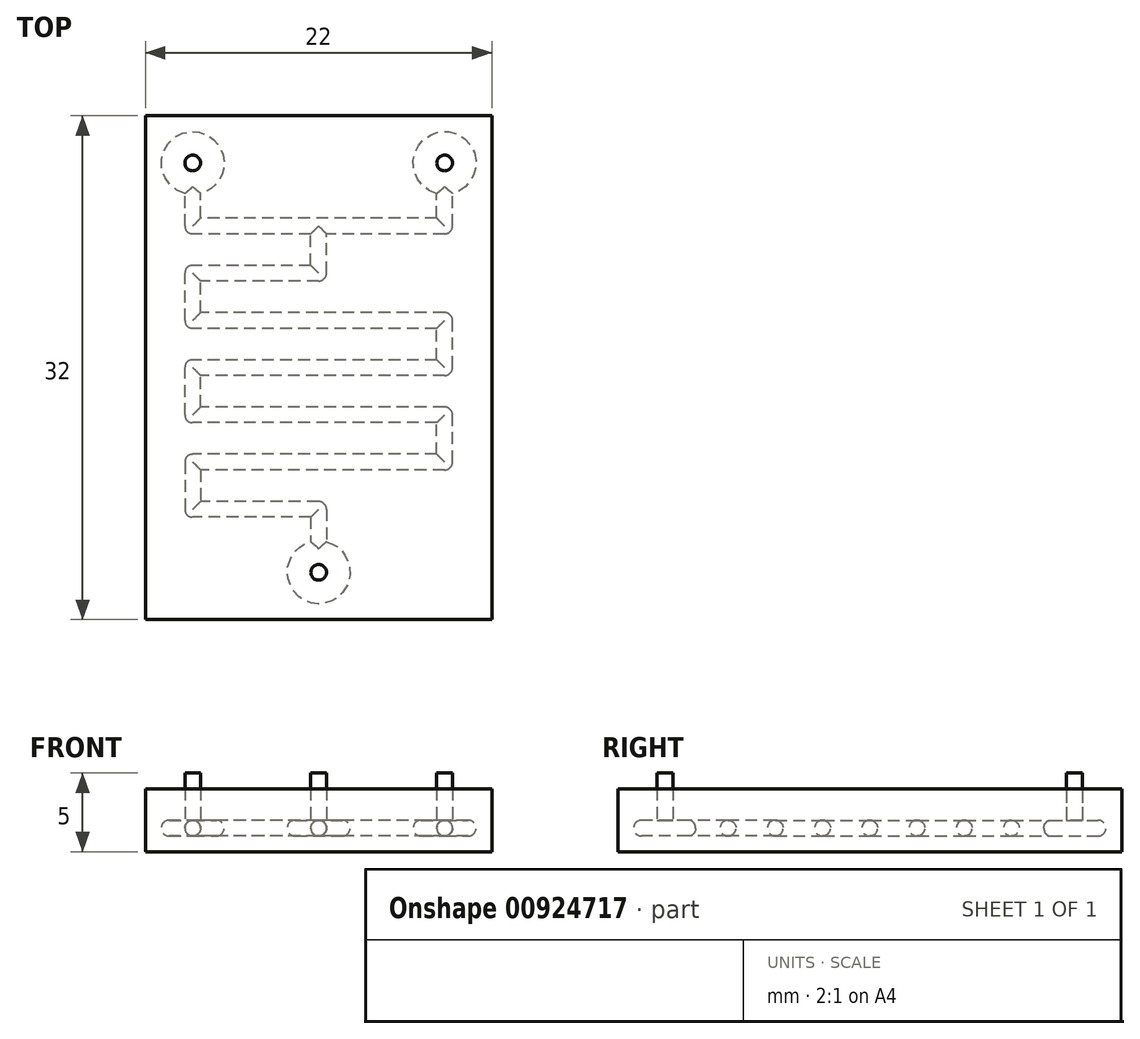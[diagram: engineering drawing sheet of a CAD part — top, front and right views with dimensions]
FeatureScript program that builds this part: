
annotation { "Feature Type Name" : "Feature", "Feature Type Description" : "" }
export const myFeature = defineFeature(function(context is Context, id is Id, definition is map)
    precondition{}
    {
        {
            var Q0;
            Q0=qCreatedBy(makeId("Top.planeOp"),FACE);
            var sketch = newSketch(context, id + "F0", { "sketchPlane" : qUnion([Q0])});
            skLineSegment(sketch, "E0.bottom", {"start": v(10, 15) * mm, "end": v(-10, 15) * mm});
            skLineSegment(sketch, "E0.top", {"start": v(10, -15) * mm, "end": v(-10, -15) * mm});
            skLineSegment(sketch, "E0.left", {"start": v(10, 15) * mm, "end": v(10, -15) * mm});
            skLineSegment(sketch, "E0.right", {"start": v(-10, 15) * mm, "end": v(-10, -15) * mm});
            skPoint(sketch, "E0.middle", {"position": v(0, 0) * mm});
            skCircle(sketch, "E1", {"center": v(-8, 13) * mm, "radius": 2 * mm});
            skCircle(sketch, "E2", {"center": v(8, 13) * mm, "radius": 2 * mm});
            skCircle(sketch, "E3", {"center": v(-8, 13) * mm, "radius": 0.5 * mm});
            skCircle(sketch, "E4", {"center": v(8, 13) * mm, "radius": 0.5 * mm});
            skCircle(sketch, "E5", {"center": v(0, -13) * mm, "radius": 2 * mm});
            skCircle(sketch, "E6", {"center": v(0, -13) * mm, "radius": 0.5 * mm});
            skSolve(sketch);
        }
        {
            var Q0;
            Q0=qCreatedBy(makeId("Top.planeOp"),FACE);
            var sketch = newSketch(context, id + "F1", { "sketchPlane" : qUnion([Q0])});
            skPoint(sketch, "E7.middle", {"position": v(0, 0) * mm});
            skLineSegment(sketch, "E8", {"start": v(-8, 9) * mm, "end": v(8, 9) * mm});
            skLineSegment(sketch, "E9", {"start": v(-8, 9) * mm, "end": v(-8, 13) * mm});
            skLineSegment(sketch, "E10", {"start": v(8, 9) * mm, "end": v(8, 13) * mm});
            skLineSegment(sketch, "E11", {"start": v(-8, 3) * mm, "end": v(-8, 6) * mm});
            skLineSegment(sketch, "E12", {"start": v(0, 9) * mm, "end": v(0, 6) * mm});
            skLineSegment(sketch, "E13", {"start": v(0, 6) * mm, "end": v(-8, 6) * mm});
            skLineSegment(sketch, "E14", {"start": v(-8, 3) * mm, "end": v(8, 3) * mm});
            skLineSegment(sketch, "E15", {"start": v(8, 3) * mm, "end": v(8, 0) * mm});
            skLineSegment(sketch, "E16", {"start": v(8, 0) * mm, "end": v(-8, 0) * mm});
            skLineSegment(sketch, "E17", {"start": v(0, -13) * mm, "end": v(0, -9) * mm});
            skLineSegment(sketch, "E18", {"start": v(0, -9) * mm, "end": v(-8, -9) * mm});
            skLineSegment(sketch, "E19", {"start": v(-8, -9) * mm, "end": v(-8, -6) * mm});
            skLineSegment(sketch, "E20", {"start": v(-8, -6) * mm, "end": v(8, -6) * mm});
            skLineSegment(sketch, "E21", {"start": v(8, -6) * mm, "end": v(8, -3) * mm});
            skLineSegment(sketch, "E22", {"start": v(8, -3) * mm, "end": v(-8, -3) * mm});
            skLineSegment(sketch, "E23", {"start": v(-8, -3) * mm, "end": v(-8, 0) * mm});
            skArc(sketch, "E24.0.startCap", {"start": v(-0.5, 9) * mm, "mid": v(0, 9.5) * mm, "end": v(0.5, 9) * mm});
            skArc(sketch, "E24.0.endCap", {"start": v(0.5, 6) * mm, "mid": v(0, 5.5) * mm, "end": v(-0.5, 6) * mm});
            skLineSegment(sketch, "E24.0.left", {"start": v(0.5, 9) * mm, "end": v(0.5, 6) * mm});
            skLineSegment(sketch, "E24.0.right", {"start": v(-0.5, 9) * mm, "end": v(-0.5, 6) * mm});
            skArc(sketch, "E25.0.startCap", {"start": v(-8, 8.5) * mm, "mid": v(-8.5, 9) * mm, "end": v(-8, 9.5) * mm});
            skArc(sketch, "E25.0.endCap", {"start": v(8, 9.5) * mm, "mid": v(8.5, 9) * mm, "end": v(8, 8.5) * mm});
            skLineSegment(sketch, "E25.0.left", {"start": v(-8, 9.5) * mm, "end": v(8, 9.5) * mm});
            skLineSegment(sketch, "E25.0.right", {"start": v(-8, 8.5) * mm, "end": v(8, 8.5) * mm});
            skArc(sketch, "E25.1.startCap", {"start": v(0, 6.5) * mm, "mid": v(0.5, 6) * mm, "end": v(0, 5.5) * mm});
            skArc(sketch, "E25.1.endCap", {"start": v(-8, 5.5) * mm, "mid": v(-8.5, 6) * mm, "end": v(-8, 6.5) * mm});
            skLineSegment(sketch, "E25.1.left", {"start": v(0, 5.5) * mm, "end": v(-8, 5.5) * mm});
            skLineSegment(sketch, "E25.1.right", {"start": v(0, 6.5) * mm, "end": v(-8, 6.5) * mm});
            skArc(sketch, "E25.2.startCap", {"start": v(-7.5, 3) * mm, "mid": v(-8, 2.5) * mm, "end": v(-8.5, 3) * mm});
            skArc(sketch, "E25.2.endCap", {"start": v(-8.5, 6) * mm, "mid": v(-8, 6.5) * mm, "end": v(-7.5, 6) * mm});
            skLineSegment(sketch, "E25.2.left", {"start": v(-8.5, 3) * mm, "end": v(-8.5, 6) * mm});
            skLineSegment(sketch, "E25.2.right", {"start": v(-7.5, 3) * mm, "end": v(-7.5, 6) * mm});
            skArc(sketch, "E25.3.startCap", {"start": v(-8, 2.5) * mm, "mid": v(-8.5, 3) * mm, "end": v(-8, 3.5) * mm});
            skArc(sketch, "E25.3.endCap", {"start": v(8, 3.5) * mm, "mid": v(8.5, 3) * mm, "end": v(8, 2.5) * mm});
            skLineSegment(sketch, "E25.3.left", {"start": v(-8, 3.5) * mm, "end": v(8, 3.5) * mm});
            skLineSegment(sketch, "E25.3.right", {"start": v(-8, 2.5) * mm, "end": v(8, 2.5) * mm});
            skArc(sketch, "E25.4.startCap", {"start": v(7.5, 3) * mm, "mid": v(8, 3.5) * mm, "end": v(8.5, 3) * mm});
            skArc(sketch, "E25.4.endCap", {"start": v(8.5, 0) * mm, "mid": v(8, -0.5) * mm, "end": v(7.5, 0) * mm});
            skLineSegment(sketch, "E25.4.left", {"start": v(8.5, 3) * mm, "end": v(8.5, 0) * mm});
            skLineSegment(sketch, "E25.4.right", {"start": v(7.5, 3) * mm, "end": v(7.5, 0) * mm});
            skArc(sketch, "E25.5.startCap", {"start": v(8, 0.5) * mm, "mid": v(8.5, 0) * mm, "end": v(8, -0.5) * mm});
            skArc(sketch, "E25.5.endCap", {"start": v(-8, -0.5) * mm, "mid": v(-8.5, 0) * mm, "end": v(-8, 0.5) * mm});
            skLineSegment(sketch, "E25.5.left", {"start": v(8, -0.5) * mm, "end": v(-8, -0.5) * mm});
            skLineSegment(sketch, "E25.5.right", {"start": v(8, 0.5) * mm, "end": v(-8, 0.5) * mm});
            skArc(sketch, "E25.6.startCap", {"start": v(-7.5, -3) * mm, "mid": v(-8, -3.5) * mm, "end": v(-8.5, -3) * mm});
            skArc(sketch, "E25.6.endCap", {"start": v(-8.5, 0) * mm, "mid": v(-8, 0.5) * mm, "end": v(-7.5, 0) * mm});
            skLineSegment(sketch, "E25.6.left", {"start": v(-8.5, -3) * mm, "end": v(-8.5, 0) * mm});
            skLineSegment(sketch, "E25.6.right", {"start": v(-7.5, -3) * mm, "end": v(-7.5, 0) * mm});
            skArc(sketch, "E25.7.startCap", {"start": v(8, -2.5) * mm, "mid": v(8.5, -3) * mm, "end": v(8, -3.5) * mm});
            skArc(sketch, "E25.7.endCap", {"start": v(-8, -3.5) * mm, "mid": v(-8.5, -3) * mm, "end": v(-8, -2.5) * mm});
            skLineSegment(sketch, "E25.7.left", {"start": v(8, -3.5) * mm, "end": v(-8, -3.5) * mm});
            skLineSegment(sketch, "E25.7.right", {"start": v(8, -2.5) * mm, "end": v(-8, -2.5) * mm});
            skArc(sketch, "E25.8.startCap", {"start": v(8.5, -6) * mm, "mid": v(8, -6.5) * mm, "end": v(7.5, -6) * mm});
            skArc(sketch, "E25.8.endCap", {"start": v(7.5, -3) * mm, "mid": v(8, -2.5) * mm, "end": v(8.5, -3) * mm});
            skLineSegment(sketch, "E25.8.left", {"start": v(7.5, -6) * mm, "end": v(7.5, -3) * mm});
            skLineSegment(sketch, "E25.8.right", {"start": v(8.5, -6) * mm, "end": v(8.5, -3) * mm});
            skArc(sketch, "E25.9.startCap", {"start": v(-8, -6.5) * mm, "mid": v(-8.5, -6) * mm, "end": v(-8, -5.5) * mm});
            skArc(sketch, "E25.9.endCap", {"start": v(8, -5.5) * mm, "mid": v(8.5, -6) * mm, "end": v(8, -6.5) * mm});
            skLineSegment(sketch, "E25.9.left", {"start": v(-8, -5.5) * mm, "end": v(8, -5.5) * mm});
            skLineSegment(sketch, "E25.9.right", {"start": v(-8, -6.5) * mm, "end": v(8, -6.5) * mm});
            skArc(sketch, "E25.10.startCap", {"start": v(-7.5, -9) * mm, "mid": v(-8, -9.5) * mm, "end": v(-8.5, -9) * mm});
            skArc(sketch, "E25.10.endCap", {"start": v(-8.5, -6) * mm, "mid": v(-8, -5.5) * mm, "end": v(-7.5, -6) * mm});
            skLineSegment(sketch, "E25.10.left", {"start": v(-8.5, -9) * mm, "end": v(-8.5, -6) * mm});
            skLineSegment(sketch, "E25.10.right", {"start": v(-7.5, -9) * mm, "end": v(-7.5, -6) * mm});
            skArc(sketch, "E25.11.startCap", {"start": v(0, -8.5) * mm, "mid": v(0.5, -9) * mm, "end": v(0, -9.5) * mm});
            skArc(sketch, "E25.11.endCap", {"start": v(-8, -9.5) * mm, "mid": v(-8.5, -9) * mm, "end": v(-8, -8.5) * mm});
            skLineSegment(sketch, "E25.11.left", {"start": v(0, -9.5) * mm, "end": v(-8, -9.5) * mm});
            skLineSegment(sketch, "E25.11.right", {"start": v(0, -8.5) * mm, "end": v(-8, -8.5) * mm});
            skArc(sketch, "E25.12.startCap", {"start": v(0.5, -13) * mm, "mid": v(0, -13.5) * mm, "end": v(-0.5, -13) * mm});
            skArc(sketch, "E25.12.endCap", {"start": v(-0.5, -9) * mm, "mid": v(0, -8.5) * mm, "end": v(0.5, -9) * mm});
            skLineSegment(sketch, "E25.12.left", {"start": v(-0.5, -13) * mm, "end": v(-0.5, -9) * mm});
            skLineSegment(sketch, "E25.12.right", {"start": v(0.5, -13) * mm, "end": v(0.5, -9) * mm});
            skArc(sketch, "E25.13.startCap", {"start": v(8.5, 9) * mm, "mid": v(8, 8.5) * mm, "end": v(7.5, 9) * mm});
            skArc(sketch, "E25.13.endCap", {"start": v(7.5, 13) * mm, "mid": v(8, 13.5) * mm, "end": v(8.5, 13) * mm});
            skLineSegment(sketch, "E25.13.left", {"start": v(7.5, 9) * mm, "end": v(7.5, 13) * mm});
            skLineSegment(sketch, "E25.13.right", {"start": v(8.5, 9) * mm, "end": v(8.5, 13) * mm});
            skArc(sketch, "E25.14.startCap", {"start": v(-7.5, 9) * mm, "mid": v(-8, 8.5) * mm, "end": v(-8.5, 9) * mm});
            skArc(sketch, "E25.14.endCap", {"start": v(-8.5, 13) * mm, "mid": v(-8, 13.5) * mm, "end": v(-7.5, 13) * mm});
            skLineSegment(sketch, "E25.14.left", {"start": v(-8.5, 9) * mm, "end": v(-8.5, 13) * mm});
            skLineSegment(sketch, "E25.14.right", {"start": v(-7.5, 9) * mm, "end": v(-7.5, 13) * mm});
            skSolve(sketch);
        }
        {
            var Q0;
            Q0=qCreatedBy(makeId("Top.planeOp"),FACE);
            var sketch = newSketch(context, id + "F2", { "sketchPlane" : qUnion([Q0])});
            skLineSegment(sketch, "E26.bottom", {"start": v(11, 16) * mm, "end": v(-11, 16) * mm});
            skLineSegment(sketch, "E26.top", {"start": v(11, -16) * mm, "end": v(-11, -16) * mm});
            skLineSegment(sketch, "E26.left", {"start": v(11, 16) * mm, "end": v(11, -16) * mm});
            skLineSegment(sketch, "E26.right", {"start": v(-11, 16) * mm, "end": v(-11, -16) * mm});
            skPoint(sketch, "E26.middle", {"position": v(0, 0) * mm});
            skSolve(sketch);
        }
        {
            var Q0;
            Q0 = qSketchRegion(id + "F1", true);
            extrude(context, id + "F3", {"entities" : qUnion([Q0]), "depth" : 1 * mm, "offsetDistance" : 25 * mm});
        }
        {
            var Q0;
            Q0=makeQuery(id+"F0.imprint","IMPRINT",FACE,{"disambiguationData":[TD([[makeQuery(id+"F0.imprint","IMPRINT",EDGE,{"derivedFrom":sQuery(id+"F0.wireOp",EDGE,"E3")}),-1.0]])]});
            var Q1;
            Q1=makeQuery(id+"F0.imprint","IMPRINT",FACE,{"disambiguationData":[TD([[makeQuery(id+"F0.imprint","IMPRINT",EDGE,{"derivedFrom":sQuery(id+"F0.wireOp",EDGE,"E5")}),1.0]])]});
            var Q2;
            Q2=makeQuery(id+"F0.imprint","IMPRINT",FACE,{"disambiguationData":[TD([[makeQuery(id+"F0.imprint","IMPRINT",EDGE,{"derivedFrom":sQuery(id+"F0.wireOp",EDGE,"E4")}),-1.0]])]});
            extrude(context, id + "F4", {"entities" : qUnion([Q0, Q1, Q2]), "operationType" : NewBodyOperationType.ADD, "depth" : 1 * mm, "offsetDistance" : 25 * mm});
        }
        {
            var Q0;
            Q0=makeQuery(id+"F0.imprint","IMPRINT",FACE,{"disambiguationData":[TD([[makeQuery(id+"F0.imprint","IMPRINT",EDGE,{"derivedFrom":sQuery(id+"F0.wireOp",EDGE,"E6")}),1.0]])]});
            var Q1;
            Q1=makeQuery(id+"F0.imprint","IMPRINT",FACE,{"disambiguationData":[TD([[makeQuery(id+"F0.imprint","IMPRINT",EDGE,{"derivedFrom":sQuery(id+"F0.wireOp",EDGE,"E4")}),1.0]])]});
            var Q2;
            Q2=makeQuery(id+"F0.imprint","IMPRINT",FACE,{"disambiguationData":[TD([[makeQuery(id+"F0.imprint","IMPRINT",EDGE,{"derivedFrom":sQuery(id+"F0.wireOp",EDGE,"E3")}),1.0]])]});
            extrude(context, id + "F5", {"entities" : qUnion([Q0, Q1, Q2]), "operationType" : NewBodyOperationType.ADD, "depth" : 4 * mm, "offsetDistance" : 25 * mm});
        }
        {
            var Q0;
            Q0 = qSketchRegion(id + "F2", true);
            extrude(context, id + "F6", {"entities" : qUnion([Q0]), "depth" : 3 * mm, "offsetDistance" : 25 * mm, "hasSecondDirection" : true, "secondDirectionOppositeDirection" : true, "secondDirectionDepth" : 1 * mm});
        }
        {
            var Q0;
            Q0=makeQuery(id+"F3.opExtrude","CAP_EDGE",EDGE,{"disambiguationData":[OSD([sQuery(id+"F1.wireOp",EDGE,"E25.9.right")])],"isStart":false});
            var Q1;
            Q1=makeQuery(id+"F3.opExtrude","CAP_EDGE",EDGE,{"disambiguationData":[OSD([sQuery(id+"F1.wireOp",EDGE,"E25.10.right")])],"isStart":false});
            var Q2;
            Q2=makeQuery(id+"F3.opExtrude","CAP_EDGE",EDGE,{"disambiguationData":[OSD([sQuery(id+"F1.wireOp",EDGE,"E25.11.right")])],"isStart":false});
            var Q3;
            Q3=makeQuery(id+"F3.opExtrude","CAP_EDGE",EDGE,{"disambiguationData":[OSD([sQuery(id+"F1.wireOp",EDGE,"E25.11.left")])],"isStart":false});
            var Q4;
            Q4=makeQuery(id+"F3.opExtrude","CAP_EDGE",EDGE,{"disambiguationData":[OSD([sQuery(id+"F1.wireOp",EDGE,"E25.7.left")])],"isStart":false});
            var Q5;
            Q5=makeQuery(id+"F3.opExtrude","CAP_EDGE",EDGE,{"disambiguationData":[OSD([sQuery(id+"F1.wireOp",EDGE,"E25.8.left")])],"isStart":false});
            var Q6;
            Q6=makeQuery(id+"F3.opExtrude","CAP_EDGE",EDGE,{"disambiguationData":[OSD([sQuery(id+"F1.wireOp",EDGE,"E25.6.right")])],"isStart":false});
            var Q7;
            Q7=makeQuery(id+"F3.opExtrude","CAP_EDGE",EDGE,{"disambiguationData":[OSD([sQuery(id+"F1.wireOp",EDGE,"E25.5.left")])],"isStart":false});
            var Q8;
            Q8=makeQuery(id+"F3.opExtrude","CAP_EDGE",EDGE,{"disambiguationData":[OSD([sQuery(id+"F1.wireOp",EDGE,"E25.4.right")])],"isStart":false});
            var Q9;
            Q9=makeQuery(id+"F3.opExtrude","CAP_EDGE",EDGE,{"disambiguationData":[OSD([sQuery(id+"F1.wireOp",EDGE,"E25.2.right")])],"isStart":false});
            var Q10;
            Q10=makeQuery(id+"F3.opExtrude","CAP_EDGE",EDGE,{"disambiguationData":[OSD([sQuery(id+"F1.wireOp",EDGE,"E25.3.right")])],"isStart":false});
            var Q11;
            Q11=makeQuery(id+"F3.opExtrude","CAP_EDGE",EDGE,{"disambiguationData":[OSD([sQuery(id+"F1.wireOp",EDGE,"E25.1.left")])],"isStart":false});
            var Q12;
            Q12=makeQuery(id+"F3.opExtrude","CAP_EDGE",EDGE,{"disambiguationData":[OSD([sQuery(id+"F1.wireOp",EDGE,"E24.0.right")])],"isStart":false});
            var Q13;
            {var subQ0=sQuery(id+"F1.wireOp",EDGE,"E25.0.right");Q13=makeQuery(id+"F3.opExtrude","CAP_EDGE",EDGE,{"disambiguationData":[OSD([subQ0]),TDD([makeQuery(id+"F1.imprint","IMPRINT",EDGE,{"disambiguationData":[TD([[makeQuery(id+"F1.imprint","INTERSECT",VERTEX,{"derivedFrom":[subQ0,sQuery(id+"F1.wireOp",EDGE,"E25.14.startCap")]}),-1.0]])],"derivedFrom":subQ0})])],"isStart":false});}
            var Q14;
            {var subQ0=sQuery(id+"F1.wireOp",EDGE,"E25.0.right");Q14=makeQuery(id+"F3.opExtrude","CAP_EDGE",EDGE,{"disambiguationData":[OSD([subQ0]),TDD([makeQuery(id+"F1.imprint","IMPRINT",EDGE,{"disambiguationData":[TD([[makeQuery(id+"F1.imprint","INTERSECT",VERTEX,{"derivedFrom":[subQ0,sQuery(id+"F1.wireOp",EDGE,"E25.13.startCap")]}),1.0]])],"derivedFrom":subQ0})])],"isStart":false});}
            var Q15;
            Q15=makeQuery(id+"F3.opExtrude","CAP_EDGE",EDGE,{"disambiguationData":[OSD([sQuery(id+"F1.wireOp",EDGE,"E25.0.left")])],"isStart":false});
            var Q16;
            Q16=makeQuery(id+"F3.opExtrude","CAP_EDGE",EDGE,{"disambiguationData":[OSD([sQuery(id+"F1.wireOp",EDGE,"E25.14.right")])],"isStart":false});
            var Q17;
            Q17=makeQuery(id+"F3.opExtrude","CAP_EDGE",EDGE,{"disambiguationData":[OSD([sQuery(id+"F1.wireOp",EDGE,"E25.13.left")])],"isStart":false});
            var Q18;
            Q18=makeQuery(id+"F3.opExtrude","CAP_EDGE",EDGE,{"disambiguationData":[OSD([sQuery(id+"F1.wireOp",EDGE,"E25.12.left")])],"isStart":false});
            var Q19;
            {var subQ0=sQuery(id+"F1.wireOp",EDGE,"E25.0.right");Q19=makeQuery(id+"F3.opExtrude","CAP_EDGE",EDGE,{"disambiguationData":[OSD([subQ0]),TDD([makeQuery(id+"F1.imprint","IMPRINT",EDGE,{"disambiguationData":[TD([[makeQuery(id+"F1.imprint","INTERSECT",VERTEX,{"derivedFrom":[subQ0,sQuery(id+"F1.wireOp",EDGE,"E25.14.startCap")]}),-1.0]])],"derivedFrom":subQ0})])],"isStart":true});}
            var Q20;
            Q20=makeQuery(id+"F3.opExtrude","CAP_EDGE",EDGE,{"disambiguationData":[OSD([sQuery(id+"F1.wireOp",EDGE,"E25.14.right")])],"isStart":true});
            var Q21;
            Q21=makeQuery(id+"F3.opExtrude","CAP_EDGE",EDGE,{"disambiguationData":[OSD([sQuery(id+"F1.wireOp",EDGE,"E25.13.left")])],"isStart":true});
            var Q22;
            Q22=makeQuery(id+"F3.opExtrude","CAP_EDGE",EDGE,{"disambiguationData":[OSD([sQuery(id+"F1.wireOp",EDGE,"E25.0.left")])],"isStart":true});
            var Q23;
            Q23=makeQuery(id+"F3.opExtrude","CAP_EDGE",EDGE,{"disambiguationData":[OSD([sQuery(id+"F1.wireOp",EDGE,"E24.0.right")])],"isStart":true});
            var Q24;
            Q24=makeQuery(id+"F3.opExtrude","CAP_EDGE",EDGE,{"disambiguationData":[OSD([sQuery(id+"F1.wireOp",EDGE,"E24.0.left")])],"isStart":true});
            var Q25;
            Q25=makeQuery(id+"F3.opExtrude","CAP_EDGE",EDGE,{"disambiguationData":[OSD([sQuery(id+"F1.wireOp",EDGE,"E25.1.right")])],"isStart":true});
            var Q26;
            Q26=makeQuery(id+"F3.opExtrude","CAP_EDGE",EDGE,{"disambiguationData":[OSD([sQuery(id+"F1.wireOp",EDGE,"E25.2.right")])],"isStart":true});
            var Q27;
            Q27=makeQuery(id+"F3.opExtrude","CAP_EDGE",EDGE,{"disambiguationData":[OSD([sQuery(id+"F1.wireOp",EDGE,"E25.3.left")])],"isStart":true});
            var Q28;
            Q28=makeQuery(id+"F3.opExtrude","CAP_EDGE",EDGE,{"disambiguationData":[OSD([sQuery(id+"F1.wireOp",EDGE,"E25.4.right")])],"isStart":true});
            var Q29;
            Q29=makeQuery(id+"F3.opExtrude","CAP_EDGE",EDGE,{"disambiguationData":[OSD([sQuery(id+"F1.wireOp",EDGE,"E25.5.right")])],"isStart":true});
            var Q30;
            Q30=makeQuery(id+"F3.opExtrude","CAP_EDGE",EDGE,{"disambiguationData":[OSD([sQuery(id+"F1.wireOp",EDGE,"E25.6.right")])],"isStart":true});
            var Q31;
            Q31=makeQuery(id+"F3.opExtrude","CAP_EDGE",EDGE,{"disambiguationData":[OSD([sQuery(id+"F1.wireOp",EDGE,"E25.7.right")])],"isStart":true});
            var Q32;
            Q32=makeQuery(id+"F3.opExtrude","CAP_EDGE",EDGE,{"disambiguationData":[OSD([sQuery(id+"F1.wireOp",EDGE,"E25.8.left")])],"isStart":true});
            var Q33;
            Q33=makeQuery(id+"F3.opExtrude","CAP_EDGE",EDGE,{"disambiguationData":[OSD([sQuery(id+"F1.wireOp",EDGE,"E25.9.left")])],"isStart":true});
            var Q34;
            Q34=makeQuery(id+"F3.opExtrude","CAP_EDGE",EDGE,{"disambiguationData":[OSD([sQuery(id+"F1.wireOp",EDGE,"E25.10.right")])],"isStart":true});
            var Q35;
            Q35=makeQuery(id+"F3.opExtrude","CAP_EDGE",EDGE,{"disambiguationData":[OSD([sQuery(id+"F1.wireOp",EDGE,"E25.11.right")])],"isStart":true});
            var Q36;
            Q36=makeQuery(id+"F3.opExtrude","CAP_EDGE",EDGE,{"disambiguationData":[OSD([sQuery(id+"F1.wireOp",EDGE,"E25.12.left")])],"isStart":true});
            var Q37;
            Q37=makeQuery(id+"F3.opExtrude","CAP_EDGE",EDGE,{"disambiguationData":[OSD([sQuery(id+"F1.wireOp",EDGE,"E25.13.right")])],"isStart":true});
            var Q38;
            Q38=makeQuery(id+"F4.opExtrude","CAP_EDGE",EDGE,{"disambiguationData":[OSD([sQuery(id+"F0.wireOp",EDGE,"E2")])],"isStart":true});
            var Q39;
            Q39=makeQuery(id+"F4.opExtrude","CAP_EDGE",EDGE,{"disambiguationData":[OSD([sQuery(id+"F0.wireOp",EDGE,"E1")])],"isStart":true});
            var Q40;
            Q40=makeQuery(id+"F4.opExtrude","CAP_EDGE",EDGE,{"disambiguationData":[OSD([sQuery(id+"F0.wireOp",EDGE,"E5")])],"isStart":true});
            var Q41;
            Q41=makeQuery(id+"F4.opExtrude","CAP_EDGE",EDGE,{"disambiguationData":[OSD([sQuery(id+"F0.wireOp",EDGE,"E1")])],"isStart":false});
            var Q42;
            Q42=makeQuery(id+"F4.opExtrude","CAP_EDGE",EDGE,{"disambiguationData":[OSD([sQuery(id+"F0.wireOp",EDGE,"E2")])],"isStart":false});
            var Q43;
            Q43=makeQuery(id+"F4.opExtrude","CAP_EDGE",EDGE,{"disambiguationData":[OSD([sQuery(id+"F0.wireOp",EDGE,"E5")])],"isStart":false});
            fillet(context, id + "F7", {"entities" : qUnion([Q0, Q1, Q2, Q3, Q4, Q5, Q6, Q7, Q8, Q9, Q10, Q11, Q12, Q13, Q14, Q15, Q16, Q17, Q18, Q19, Q20, Q21, Q22, Q23, Q24, Q25, Q26, Q27, Q28, Q29, Q30, Q31, Q32, Q33, Q34, Q35, Q36, Q37, Q38, Q39, Q40, Q41, Q42, Q43]), "radius" : .5 * mm, "tangentPropagation" : true, "allowEdgeOverflow" : false});
        }
    });
